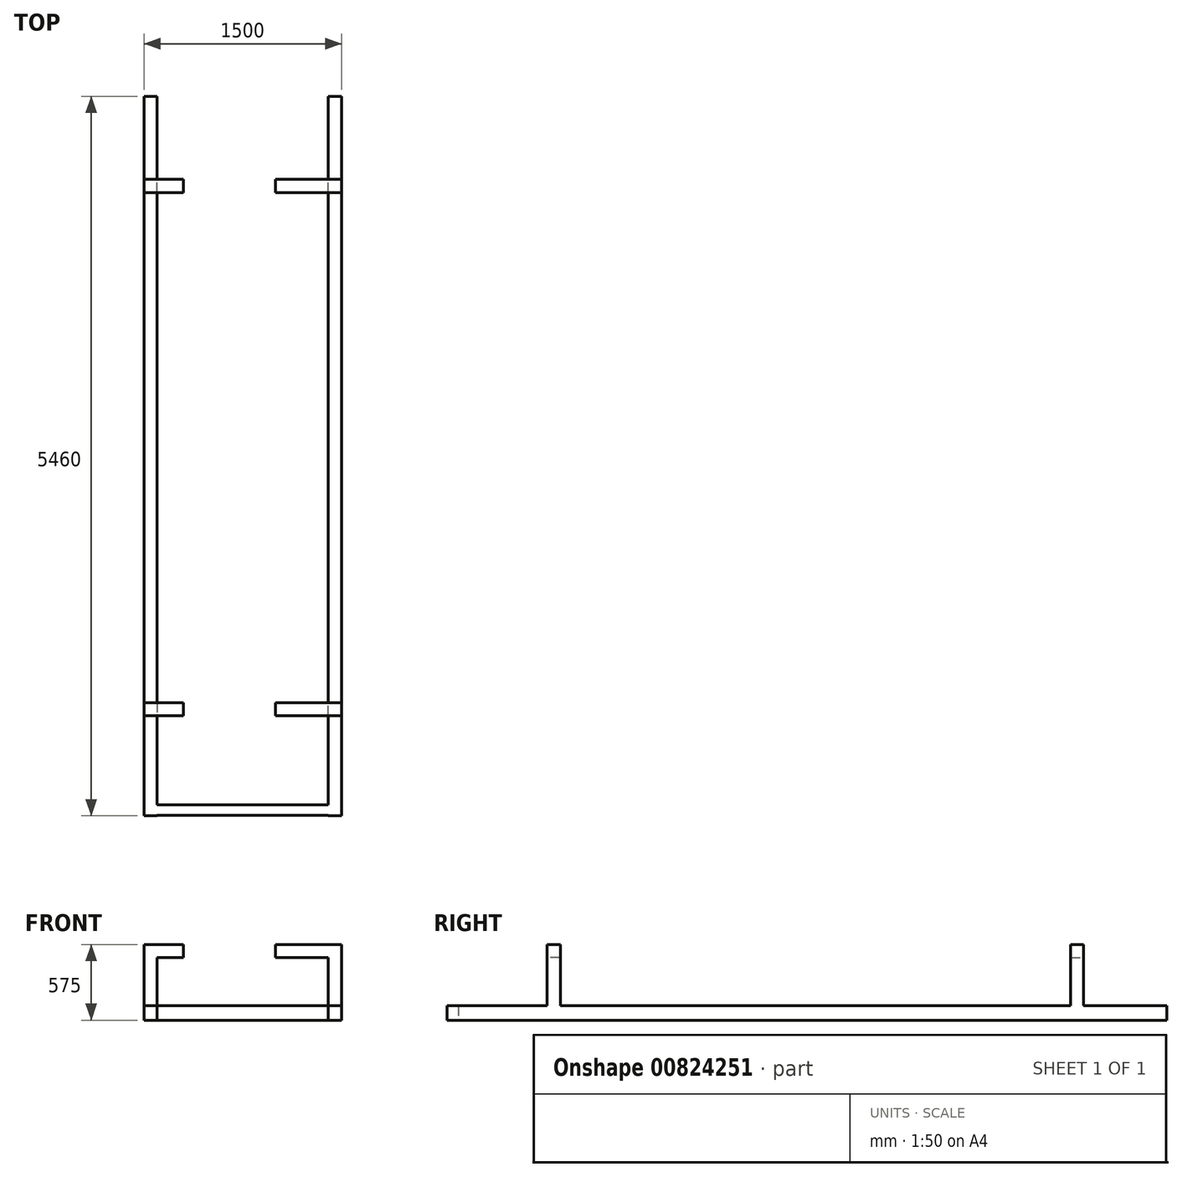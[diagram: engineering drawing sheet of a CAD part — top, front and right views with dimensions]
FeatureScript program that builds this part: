
annotation { "Feature Type Name" : "Feature", "Feature Type Description" : "" }
export const myFeature = defineFeature(function(context is Context, id is Id, definition is map)
    precondition{}
    {
        {
            var Q0;
            Q0=qCreatedBy(makeId("Top.planeOp"),FACE);
            var sketch = newSketch(context, id + "F0", { "sketchPlane" : qUnion([Q0])});
            skLineSegment(sketch, "E0.bottom", {"start": v(750, -2850) * mm, "end": v(650, -2850) * mm});
            skLineSegment(sketch, "E0.top", {"start": v(750, 2850) * mm, "end": v(650, 2850) * mm});
            skLineSegment(sketch, "E0.left", {"start": v(750, -2850) * mm, "end": v(750, 2850) * mm});
            skLineSegment(sketch, "E0.right", {"start": v(-750, -2850) * mm, "end": v(-750, 2850) * mm});
            skPoint(sketch, "E0.middle", {"position": v(0, 0) * mm});
            skLineSegment(sketch, "E1.left", {"start": v(-650, 2850) * mm, "end": v(-650, -2850) * mm});
            skLineSegment(sketch, "E1.right", {"start": v(650, 2850) * mm, "end": v(650, -2850) * mm});
            skLineSegment(sketch, "E2.trimOffspring", {"start": v(-650, 2850) * mm, "end": v(-750, 2850) * mm});
            skLineSegment(sketch, "E3.trimOffspring", {"start": v(-650, -2850) * mm, "end": v(-750, -2850) * mm});
            skSolve(sketch);
        }
        {
            var Q0;
            Q0 = qSketchRegion(id + "F0", true);
            extrude(context, id + "F1", {"entities" : qUnion([Q0]), "depth" : 110 * mm, "offsetDistance" : 25 * mm});
        }
        {
            var Q0;
            Q0=makeQuery(id+"F1.opExtrude","SWEPT_FACE",FACE,{"disambiguationData":[OSD([sQuery(id+"F0.wireOp",EDGE,"E1.left")])]});
            var sketch = newSketch(context, id + "F2", { "sketchPlane" : qUnion([Q0])});
            skLineSegment(sketch, "E4.bottom", {"start": v(-2604.7, 110) * mm, "end": v(-2524.7, 110) * mm});
            skLineSegment(sketch, "E4.top", {"start": v(-2604.7, 0) * mm, "end": v(-2524.7, 0) * mm});
            skLineSegment(sketch, "E4.left", {"start": v(-2604.7, 110) * mm, "end": v(-2604.7, 0) * mm});
            skLineSegment(sketch, "E4.right", {"start": v(-2524.7, 110) * mm, "end": v(-2524.7, 0) * mm});
            skSolve(sketch);
        }
        {
            var Q0;
            Q0=makeQuery(id+"F2.imprint","IMPRINT",FACE,{"disambiguationData":[TD([[makeQuery(id+"F2.imprint","IMPRINT",EDGE,{"derivedFrom":sQuery(id+"F2.wireOp",EDGE,"E4.bottom")}),1.0]])]});
            extrude(context, id + "F3", {"entities" : qUnion([Q0]), "operationType" : NewBodyOperationType.ADD, "depth" : 1350 * mm, "offsetDistance" : 25 * mm});
        }
        {
            var Q0;
            Q0=makeQuery(id+"F3.boolean.opBoolean","MERGE",FACE,{"derivedFrom":[makeQuery(id+"F1.opExtrude","CAP_FACE",FACE,{"disambiguationData":[OSD([sQuery(id+"F0.wireOp",EDGE,"E0.bottom"),sQuery(id+"F0.wireOp",EDGE,"E0.top"),sQuery(id+"F0.wireOp",EDGE,"E0.left"),sQuery(id+"F0.wireOp",EDGE,"E1.right")])],"isStart":false}),makeQuery(id+"F1.opExtrude","CAP_FACE",FACE,{"disambiguationData":[OSD([sQuery(id+"F0.wireOp",EDGE,"E0.right"),sQuery(id+"F0.wireOp",EDGE,"E1.left"),sQuery(id+"F0.wireOp",EDGE,"E2.trimOffspring"),sQuery(id+"F0.wireOp",EDGE,"E3.trimOffspring")])],"isStart":false}),makeQuery(id+"F3.opExtrude","SWEPT_FACE",FACE,{"disambiguationData":[OSD([sQuery(id+"F2.wireOp",EDGE,"E4.bottom")])]})]});
            var sketch = newSketch(context, id + "F4", { "sketchPlane" : qUnion([Q0])});
            skLineSegment(sketch, "E5.bottom", {"start": v(650, -1850) * mm, "end": v(750, -1850) * mm});
            skLineSegment(sketch, "E5.top", {"start": v(650, -1750) * mm, "end": v(750, -1750) * mm});
            skLineSegment(sketch, "E5.left", {"start": v(650, -1850) * mm, "end": v(650, -1750) * mm});
            skLineSegment(sketch, "E5.right", {"start": v(750, -1850) * mm, "end": v(750, -1750) * mm});
            skLineSegment(sketch, "E6.0.1.0", {"start": v(750, 2120) * mm, "end": v(750, 2220) * mm});
            skLineSegment(sketch, "E6.0.1.1", {"start": v(650, 2120) * mm, "end": v(650, 2220) * mm});
            skLineSegment(sketch, "E6.0.1.2", {"start": v(650, 2220) * mm, "end": v(750, 2220) * mm});
            skLineSegment(sketch, "E6.0.1.3", {"start": v(650, 2120) * mm, "end": v(750, 2120) * mm});
            skLineSegment(sketch, "E6.1.0.0", {"start": v(-650, -1850) * mm, "end": v(-650, -1750) * mm});
            skLineSegment(sketch, "E6.1.0.1", {"start": v(-750, -1850) * mm, "end": v(-750, -1750) * mm});
            skLineSegment(sketch, "E6.1.0.2", {"start": v(-750, -1750) * mm, "end": v(-650, -1750) * mm});
            skLineSegment(sketch, "E6.1.0.3", {"start": v(-750, -1850) * mm, "end": v(-650, -1850) * mm});
            skLineSegment(sketch, "E6.1.1.0", {"start": v(-650, 2120) * mm, "end": v(-650, 2220) * mm});
            skLineSegment(sketch, "E6.1.1.1", {"start": v(-750, 2120) * mm, "end": v(-750, 2220) * mm});
            skLineSegment(sketch, "E6.1.1.2", {"start": v(-750, 2220) * mm, "end": v(-650, 2220) * mm});
            skLineSegment(sketch, "E6.1.1.3", {"start": v(-750, 2120) * mm, "end": v(-650, 2120) * mm});
            skLineSegment(sketch, "E6.direction1", {"start": v(650, -1850) * mm, "end": v(-750, -1850) * mm, "construction": true});
            skLineSegment(sketch, "E6.direction2", {"start": v(650, -1850) * mm, "end": v(650, 2120) * mm, "construction": true});
            skSolve(sketch);
        }
        {
            var Q0;
            Q0 = qSketchRegion(id + "F4", true);
            extrude(context, id + "F5", {"entities" : qUnion([Q0]), "operationType" : NewBodyOperationType.ADD, "depth" : 465 * mm, "offsetDistance" : 25 * mm});
        }
        {
            var Q0;
            Q0=makeQuery(id+"F1.opExtrude","SWEPT_FACE",FACE,{"disambiguationData":[OSD([sQuery(id+"F0.wireOp",EDGE,"E0.bottom")])]});
            var Q1;
            Q1=makeQuery(id+"F1.opExtrude","SWEPT_FACE",FACE,{"disambiguationData":[OSD([sQuery(id+"F0.wireOp",EDGE,"E3.trimOffspring")])]});
            extrude(context, id + "F6", {"entities" : qUnion([Q0, Q1]), "operationType" : NewBodyOperationType.REMOVE, "oppositeDirection" : true, "depth" : 240 * mm, "offsetDistance" : 25 * mm});
        }
        {
            var Q0;
            {var subQ1=sQuery(id+"F0.wireOp",EDGE,"E2.trimOffspring");var subQ2=sQuery(id+"F0.wireOp",EDGE,"E1.left");Q0=makeQuery(id+"F5.boolean.opBoolean","MERGE",FACE,{"derivedFrom":[makeQuery(id+"F3.boolean.opBoolean","SPLIT",FACE,{"disambiguationData":[TD([makeQuery(id+"F1.opExtrude","SWEPT_FACE",FACE,{"disambiguationData":[OSD([subQ1])]})])],"derivedFrom":makeQuery(id+"F1.opExtrude","SWEPT_FACE",FACE,{"disambiguationData":[OSD([subQ2])]})}),makeQuery(id+"F5.opExtrude","SWEPT_FACE",FACE,{"disambiguationData":[OSD([sQuery(id+"F4.wireOp",EDGE,"E6.1.0.0")])]}),makeQuery(id+"F5.opExtrude","SWEPT_FACE",FACE,{"disambiguationData":[OSD([sQuery(id+"F4.wireOp",EDGE,"E6.1.1.0")])]})]});}
            var sketch = newSketch(context, id + "F7", { "sketchPlane" : qUnion([Q0])});
            skLineSegment(sketch, "E7.bottom", {"start": v(2120, 575) * mm, "end": v(2220, 575) * mm});
            skLineSegment(sketch, "E7.top", {"start": v(2120, 475) * mm, "end": v(2220, 475) * mm});
            skLineSegment(sketch, "E7.left", {"start": v(2120, 575) * mm, "end": v(2120, 475) * mm});
            skLineSegment(sketch, "E7.right", {"start": v(2220, 575) * mm, "end": v(2220, 475) * mm});
            skSolve(sketch);
        }
        {
            var Q0;
            Q0=makeQuery(id+"F7.imprint","IMPRINT",FACE,{"disambiguationData":[TD([[makeQuery(id+"F7.imprint","IMPRINT",EDGE,{"derivedFrom":sQuery(id+"F7.wireOp",EDGE,"E7.bottom")}),1.0]])]});
            extrude(context, id + "F8", {"entities" : qUnion([Q0]), "operationType" : NewBodyOperationType.ADD, "depth" : 200 * mm, "offsetDistance" : 25 * mm});
        }
        {
            var Q0;
            {var subQ0=sQuery(id+"F0.wireOp",EDGE,"E0.top");var subQ1=sQuery(id+"F0.wireOp",EDGE,"E1.right");Q0=makeQuery(id+"F5.boolean.opBoolean","MERGE",FACE,{"derivedFrom":[makeQuery(id+"F3.boolean.opBoolean","SPLIT",FACE,{"disambiguationData":[TD([makeQuery(id+"F1.opExtrude","SWEPT_FACE",FACE,{"disambiguationData":[OSD([subQ0])]})])],"derivedFrom":makeQuery(id+"F1.opExtrude","SWEPT_FACE",FACE,{"disambiguationData":[OSD([subQ1])]})}),makeQuery(id+"F5.opExtrude","SWEPT_FACE",FACE,{"disambiguationData":[OSD([sQuery(id+"F4.wireOp",EDGE,"E5.left")])]}),makeQuery(id+"F5.opExtrude","SWEPT_FACE",FACE,{"disambiguationData":[OSD([sQuery(id+"F4.wireOp",EDGE,"E6.0.1.1")])]})]});}
            var sketch = newSketch(context, id + "F9", { "sketchPlane" : qUnion([Q0])});
            skLineSegment(sketch, "E8.bottom", {"start": v(-2120, 575) * mm, "end": v(-2220, 575) * mm});
            skLineSegment(sketch, "E8.top", {"start": v(-2120, 475) * mm, "end": v(-2220, 475) * mm});
            skLineSegment(sketch, "E8.left", {"start": v(-2120, 575) * mm, "end": v(-2120, 475) * mm});
            skLineSegment(sketch, "E8.right", {"start": v(-2220, 575) * mm, "end": v(-2220, 475) * mm});
            skLineSegment(sketch, "E9.bottom", {"start": v(1850, 575) * mm, "end": v(1750, 575) * mm});
            skLineSegment(sketch, "E9.top", {"start": v(1850, 475) * mm, "end": v(1750, 475) * mm});
            skLineSegment(sketch, "E9.left", {"start": v(1850, 575) * mm, "end": v(1850, 475) * mm});
            skLineSegment(sketch, "E9.right", {"start": v(1750, 575) * mm, "end": v(1750, 475) * mm});
            skSolve(sketch);
        }
        {
            var Q0;
            Q0 = qSketchRegion(id + "F9", true);
            extrude(context, id + "F10", {"entities" : qUnion([Q0]), "operationType" : NewBodyOperationType.ADD, "depth" : 400 * mm, "offsetDistance" : 25 * mm});
        }
        {
            var Q0;
            {var subQ1=sQuery(id+"F0.wireOp",EDGE,"E2.trimOffspring");var subQ2=sQuery(id+"F0.wireOp",EDGE,"E1.left");Q0=makeQuery(id+"F5.boolean.opBoolean","MERGE",FACE,{"derivedFrom":[makeQuery(id+"F3.boolean.opBoolean","SPLIT",FACE,{"disambiguationData":[TD([makeQuery(id+"F1.opExtrude","SWEPT_FACE",FACE,{"disambiguationData":[OSD([subQ1])]})])],"derivedFrom":makeQuery(id+"F1.opExtrude","SWEPT_FACE",FACE,{"disambiguationData":[OSD([subQ2])]})}),makeQuery(id+"F5.opExtrude","SWEPT_FACE",FACE,{"disambiguationData":[OSD([sQuery(id+"F4.wireOp",EDGE,"E6.1.0.0")])]}),makeQuery(id+"F5.opExtrude","SWEPT_FACE",FACE,{"disambiguationData":[OSD([sQuery(id+"F4.wireOp",EDGE,"E6.1.1.0")])]})]});}
            var sketch = newSketch(context, id + "F11", { "sketchPlane" : qUnion([Q0])});
            skLineSegment(sketch, "E10.bottom", {"start": v(-1750, 575) * mm, "end": v(-1850, 575) * mm});
            skLineSegment(sketch, "E10.top", {"start": v(-1750, 475) * mm, "end": v(-1850, 475) * mm});
            skLineSegment(sketch, "E10.left", {"start": v(-1750, 575) * mm, "end": v(-1750, 475) * mm});
            skLineSegment(sketch, "E10.right", {"start": v(-1850, 575) * mm, "end": v(-1850, 475) * mm});
            skSolve(sketch);
        }
        {
            var Q0;
            Q0 = qSketchRegion(id + "F11", true);
            extrude(context, id + "F12", {"entities" : qUnion([Q0]), "operationType" : NewBodyOperationType.ADD, "depth" : 200 * mm, "offsetDistance" : 25 * mm});
        }
    });
